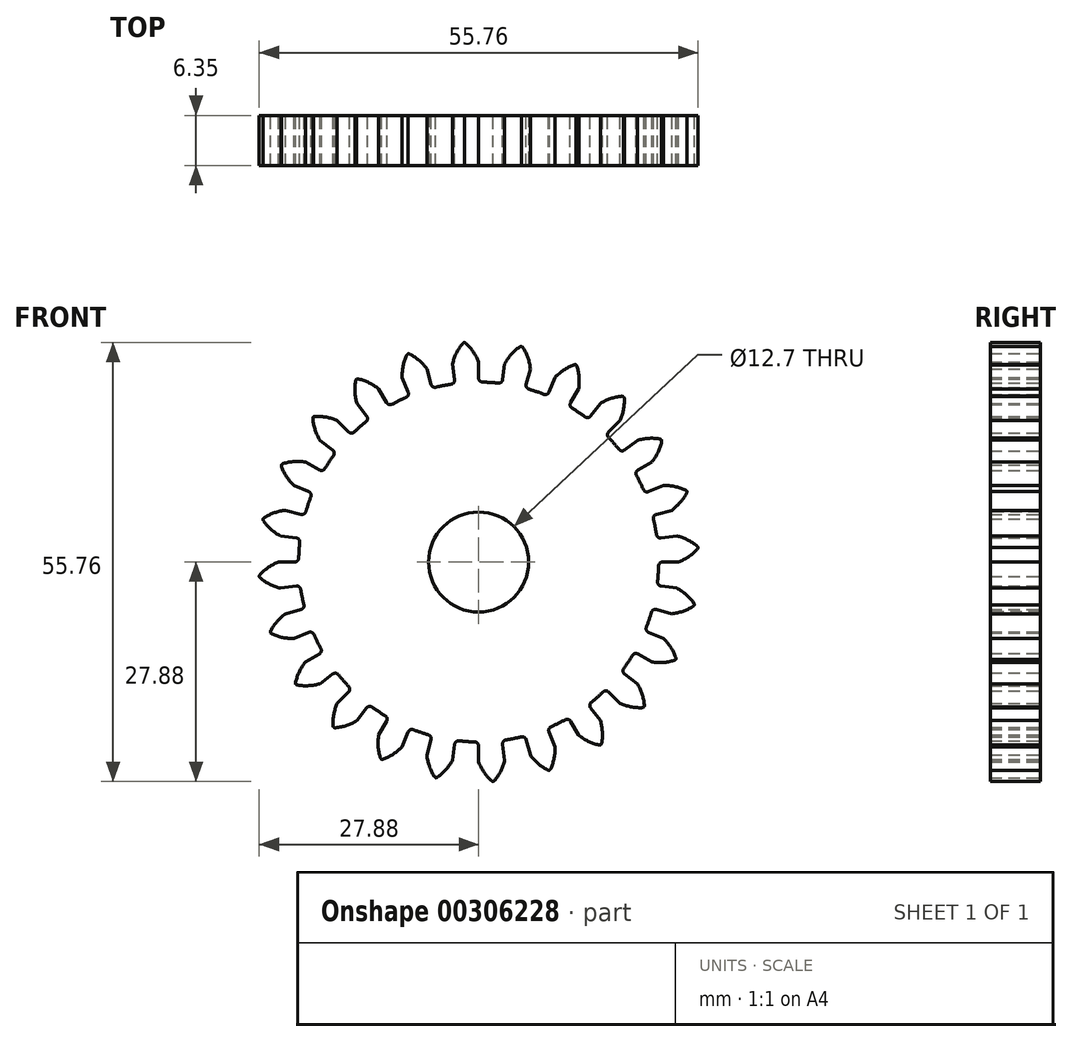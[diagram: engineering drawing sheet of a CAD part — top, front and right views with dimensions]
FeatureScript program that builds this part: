
annotation { "Feature Type Name" : "Feature", "Feature Type Description" : "" }
export const myFeature = defineFeature(function(context is Context, id is Id, definition is map)
    precondition{}
    {
        {
            var Q0;
            Q0=qCreatedBy(makeId("Front.planeOp"),FACE);
            var sketch = newSketch(context, id + "F0", { "sketchPlane" : qUnion([Q0])});
            skArc(sketch, "E0", {"start": v(-3.48, 22.6) * mm, "mid": v(1.5, -22.81) * mm, "end": v(0.5, 22.85) * mm});
            skLineSegment(sketch, "E1", {"start": v(0, 0) * mm, "end": v(-3, 45.83) * mm, "construction": true});
            skArc(sketch, "E2.trimOffspring", {"start": v(0, 25.4) * mm, "mid": v(-0.66, 26.66) * mm, "end": v(-1.58, 27.75) * mm});
            skLineSegment(sketch, "E3", {"start": v(0, 25.4) * mm, "end": v(0, 23.36) * mm});
            skArc(sketch, "E4.MirrorCS", {"start": v(-3.32, 25.18) * mm, "mid": v(-2.83, 26.52) * mm, "end": v(-2.06, 27.72) * mm});
            skLineSegment(sketch, "E5.MirrorCS", {"start": v(-3.32, 25.18) * mm, "end": v(-3.05, 23.16) * mm});
            skPoint(sketch, "E6.visualSharp", {"position": v(-1.92, 27.87) * mm});
            skArc(sketch, "E6.filletArc", {"start": v(-1.83, 27.88) * mm, "mid": v(-1.95, 27.81) * mm, "end": v(-2.06, 27.72) * mm});
            skPoint(sketch, "E7.visualSharp", {"position": v(-1.73, 27.89) * mm});
            skArc(sketch, "E7.filletArc", {"start": v(-1.58, 27.75) * mm, "mid": v(-1.7, 27.83) * mm, "end": v(-1.83, 27.88) * mm});
            skPoint(sketch, "E8.orphan", {"position": v(-2.55, 19.37) * mm});
            skPoint(sketch, "E9.orphan", {"position": v(0, 19.54) * mm});
            skPoint(sketch, "E10.visualSharp", {"position": v(-2.98, 22.66) * mm});
            skArc(sketch, "E10.filletArc", {"start": v(-3.48, 22.6) * mm, "mid": v(-3.15, 22.8) * mm, "end": v(-3.05, 23.16) * mm});
            skPoint(sketch, "E11.visualSharp", {"position": v(0, 22.86) * mm});
            skArc(sketch, "E11.filletArc", {"start": v(0, 23.36) * mm, "mid": v(0.14, 23) * mm, "end": v(0.5, 22.85) * mm});
            skPoint(sketch, "E12.MirrorCS.end.orphan", {"position": v(-1.83, 27.89) * mm});
            skArc(sketch, "E13.1.0", {"start": v(-6.57, 24.53) * mm, "mid": v(-7.54, 25.58) * mm, "end": v(-8.7, 26.4) * mm});
            skArc(sketch, "E13.1.1", {"start": v(-8.7, 26.4) * mm, "mid": v(-8.84, 26.44) * mm, "end": v(-8.98, 26.45) * mm});
            skArc(sketch, "E13.1.2", {"start": v(-8.98, 26.45) * mm, "mid": v(-9.08, 26.36) * mm, "end": v(-9.16, 26.24) * mm});
            skArc(sketch, "E13.1.3", {"start": v(-9.72, 23.47) * mm, "mid": v(-9.6, 24.89) * mm, "end": v(-9.16, 26.24) * mm});
            skLineSegment(sketch, "E13.1.4", {"start": v(-9.72, 23.47) * mm, "end": v(-8.94, 21.58) * mm});
            skArc(sketch, "E13.1.5", {"start": v(-9.2, 20.92) * mm, "mid": v(-8.94, 21.2) * mm, "end": v(-8.94, 21.58) * mm});
            skArc(sketch, "E13.1.6", {"start": v(-6.05, 22.57) * mm, "mid": v(-5.81, 22.26) * mm, "end": v(-5.44, 22.2) * mm});
            skLineSegment(sketch, "E13.1.7", {"start": v(-6.57, 24.53) * mm, "end": v(-6.05, 22.57) * mm});
            skArc(sketch, "E13.2.0", {"start": v(-12.7, 22) * mm, "mid": v(-13.9, 22.76) * mm, "end": v(-15.24, 23.24) * mm});
            skArc(sketch, "E13.2.1", {"start": v(-15.24, 23.24) * mm, "mid": v(-15.38, 23.25) * mm, "end": v(-15.52, 23.23) * mm});
            skArc(sketch, "E13.2.2", {"start": v(-15.52, 23.23) * mm, "mid": v(-15.6, 23.11) * mm, "end": v(-15.64, 22.98) * mm});
            skArc(sketch, "E13.2.3", {"start": v(-15.46, 20.15) * mm, "mid": v(-15.71, 21.55) * mm, "end": v(-15.64, 22.98) * mm});
            skLineSegment(sketch, "E13.2.4", {"start": v(-15.46, 20.15) * mm, "end": v(-14.22, 18.53) * mm});
            skArc(sketch, "E13.2.5", {"start": v(-14.3, 17.83) * mm, "mid": v(-14.12, 18.16) * mm, "end": v(-14.22, 18.53) * mm});
            skArc(sketch, "E13.2.6", {"start": v(-11.68, 20.23) * mm, "mid": v(-11.38, 20) * mm, "end": v(-11, 20.04) * mm});
            skLineSegment(sketch, "E13.2.7", {"start": v(-12.7, 22) * mm, "end": v(-11.68, 20.23) * mm});
            skArc(sketch, "E13.3.0", {"start": v(-17.96, 17.96) * mm, "mid": v(-19.32, 18.39) * mm, "end": v(-20.74, 18.5) * mm});
            skArc(sketch, "E13.3.1", {"start": v(-20.74, 18.5) * mm, "mid": v(-20.88, 18.48) * mm, "end": v(-21, 18.42) * mm});
            skArc(sketch, "E13.3.2", {"start": v(-21, 18.42) * mm, "mid": v(-21.05, 18.29) * mm, "end": v(-21.05, 18.14) * mm});
            skArc(sketch, "E13.3.3", {"start": v(-20.15, 15.46) * mm, "mid": v(-20.75, 16.75) * mm, "end": v(-21.05, 18.14) * mm});
            skLineSegment(sketch, "E13.3.4", {"start": v(-20.15, 15.46) * mm, "end": v(-18.53, 14.22) * mm});
            skArc(sketch, "E13.3.5", {"start": v(-18.43, 13.52) * mm, "mid": v(-18.34, 13.9) * mm, "end": v(-18.53, 14.22) * mm});
            skArc(sketch, "E13.3.6", {"start": v(-16.52, 16.52) * mm, "mid": v(-16.17, 16.37) * mm, "end": v(-15.8, 16.51) * mm});
            skLineSegment(sketch, "E13.3.7", {"start": v(-17.96, 17.96) * mm, "end": v(-16.52, 16.52) * mm});
            skArc(sketch, "E13.4.0", {"start": v(-22, 12.7) * mm, "mid": v(-23.42, 12.76) * mm, "end": v(-24.82, 12.5) * mm});
            skArc(sketch, "E13.4.1", {"start": v(-24.82, 12.5) * mm, "mid": v(-24.95, 12.45) * mm, "end": v(-25.06, 12.36) * mm});
            skArc(sketch, "E13.4.2", {"start": v(-25.06, 12.36) * mm, "mid": v(-25.06, 12.22) * mm, "end": v(-25.03, 12.08) * mm});
            skArc(sketch, "E13.4.3", {"start": v(-23.47, 9.72) * mm, "mid": v(-24.38, 10.81) * mm, "end": v(-25.03, 12.08) * mm});
            skLineSegment(sketch, "E13.4.4", {"start": v(-23.47, 9.72) * mm, "end": v(-21.58, 8.94) * mm});
            skArc(sketch, "E13.4.5", {"start": v(-21.3, 8.29) * mm, "mid": v(-21.31, 8.67) * mm, "end": v(-21.58, 8.94) * mm});
            skArc(sketch, "E13.4.6", {"start": v(-20.23, 11.68) * mm, "mid": v(-19.85, 11.63) * mm, "end": v(-19.54, 11.86) * mm});
            skLineSegment(sketch, "E13.4.7", {"start": v(-22, 12.7) * mm, "end": v(-20.23, 11.68) * mm});
            skArc(sketch, "E13.5.0", {"start": v(-24.53, 6.57) * mm, "mid": v(-25.92, 6.27) * mm, "end": v(-27.21, 5.66) * mm});
            skArc(sketch, "E13.5.1", {"start": v(-27.21, 5.66) * mm, "mid": v(-27.32, 5.57) * mm, "end": v(-27.4, 5.45) * mm});
            skArc(sketch, "E13.5.2", {"start": v(-27.4, 5.45) * mm, "mid": v(-27.37, 5.31) * mm, "end": v(-27.3, 5.19) * mm});
            skArc(sketch, "E13.5.3", {"start": v(-25.18, 3.32) * mm, "mid": v(-26.35, 4.13) * mm, "end": v(-27.3, 5.19) * mm});
            skLineSegment(sketch, "E13.5.4", {"start": v(-25.18, 3.32) * mm, "end": v(-23.16, 3.05) * mm});
            skArc(sketch, "E13.5.5", {"start": v(-22.72, 2.5) * mm, "mid": v(-22.83, 2.86) * mm, "end": v(-23.16, 3.05) * mm});
            skArc(sketch, "E13.5.6", {"start": v(-22.57, 6.05) * mm, "mid": v(-22.19, 6.1) * mm, "end": v(-21.95, 6.4) * mm});
            skLineSegment(sketch, "E13.5.7", {"start": v(-24.53, 6.57) * mm, "end": v(-22.57, 6.05) * mm});
            skArc(sketch, "E13.6.0", {"start": v(-25.4, 0) * mm, "mid": v(-26.66, -0.66) * mm, "end": v(-27.75, -1.58) * mm});
            skArc(sketch, "E13.6.1", {"start": v(-27.75, -1.58) * mm, "mid": v(-27.83, -1.7) * mm, "end": v(-27.88, -1.83) * mm});
            skArc(sketch, "E13.6.2", {"start": v(-27.88, -1.83) * mm, "mid": v(-27.81, -1.95) * mm, "end": v(-27.72, -2.06) * mm});
            skArc(sketch, "E13.6.3", {"start": v(-25.18, -3.32) * mm, "mid": v(-26.52, -2.83) * mm, "end": v(-27.72, -2.06) * mm});
            skLineSegment(sketch, "E13.6.4", {"start": v(-25.18, -3.32) * mm, "end": v(-23.16, -3.05) * mm});
            skArc(sketch, "E13.6.5", {"start": v(-22.6, -3.48) * mm, "mid": v(-22.8, -3.15) * mm, "end": v(-23.16, -3.05) * mm});
            skArc(sketch, "E13.6.6", {"start": v(-23.36, 0) * mm, "mid": v(-23, 0.14) * mm, "end": v(-22.85, 0.5) * mm});
            skLineSegment(sketch, "E13.6.7", {"start": v(-25.4, 0) * mm, "end": v(-23.36, 0) * mm});
            skArc(sketch, "E13.7.0", {"start": v(-24.53, -6.57) * mm, "mid": v(-25.58, -7.54) * mm, "end": v(-26.4, -8.7) * mm});
            skArc(sketch, "E13.7.1", {"start": v(-26.4, -8.7) * mm, "mid": v(-26.44, -8.84) * mm, "end": v(-26.45, -8.98) * mm});
            skArc(sketch, "E13.7.2", {"start": v(-26.45, -8.98) * mm, "mid": v(-26.36, -9.08) * mm, "end": v(-26.24, -9.16) * mm});
            skArc(sketch, "E13.7.3", {"start": v(-23.47, -9.72) * mm, "mid": v(-24.89, -9.6) * mm, "end": v(-26.24, -9.16) * mm});
            skLineSegment(sketch, "E13.7.4", {"start": v(-23.47, -9.72) * mm, "end": v(-21.58, -8.94) * mm});
            skArc(sketch, "E13.7.5", {"start": v(-20.92, -9.2) * mm, "mid": v(-21.2, -8.94) * mm, "end": v(-21.58, -8.94) * mm});
            skArc(sketch, "E13.7.6", {"start": v(-22.57, -6.05) * mm, "mid": v(-22.26, -5.81) * mm, "end": v(-22.2, -5.44) * mm});
            skLineSegment(sketch, "E13.7.7", {"start": v(-24.53, -6.57) * mm, "end": v(-22.57, -6.05) * mm});
            skArc(sketch, "E13.8.0", {"start": v(-22, -12.7) * mm, "mid": v(-22.76, -13.9) * mm, "end": v(-23.24, -15.24) * mm});
            skArc(sketch, "E13.8.1", {"start": v(-23.24, -15.24) * mm, "mid": v(-23.25, -15.38) * mm, "end": v(-23.23, -15.52) * mm});
            skArc(sketch, "E13.8.2", {"start": v(-23.23, -15.52) * mm, "mid": v(-23.11, -15.6) * mm, "end": v(-22.98, -15.64) * mm});
            skArc(sketch, "E13.8.3", {"start": v(-20.15, -15.46) * mm, "mid": v(-21.55, -15.71) * mm, "end": v(-22.98, -15.64) * mm});
            skLineSegment(sketch, "E13.8.4", {"start": v(-20.15, -15.46) * mm, "end": v(-18.53, -14.22) * mm});
            skArc(sketch, "E13.8.5", {"start": v(-17.83, -14.3) * mm, "mid": v(-18.16, -14.12) * mm, "end": v(-18.53, -14.22) * mm});
            skArc(sketch, "E13.8.6", {"start": v(-20.23, -11.68) * mm, "mid": v(-20, -11.38) * mm, "end": v(-20.04, -11) * mm});
            skLineSegment(sketch, "E13.8.7", {"start": v(-22, -12.7) * mm, "end": v(-20.23, -11.68) * mm});
            skArc(sketch, "E13.9.0", {"start": v(-17.96, -17.96) * mm, "mid": v(-18.39, -19.32) * mm, "end": v(-18.5, -20.74) * mm});
            skArc(sketch, "E13.9.1", {"start": v(-18.5, -20.74) * mm, "mid": v(-18.48, -20.88) * mm, "end": v(-18.42, -21) * mm});
            skArc(sketch, "E13.9.2", {"start": v(-18.42, -21) * mm, "mid": v(-18.29, -21.05) * mm, "end": v(-18.14, -21.05) * mm});
            skArc(sketch, "E13.9.3", {"start": v(-15.46, -20.15) * mm, "mid": v(-16.75, -20.75) * mm, "end": v(-18.14, -21.05) * mm});
            skLineSegment(sketch, "E13.9.4", {"start": v(-15.46, -20.15) * mm, "end": v(-14.22, -18.53) * mm});
            skArc(sketch, "E13.9.5", {"start": v(-13.52, -18.43) * mm, "mid": v(-13.9, -18.34) * mm, "end": v(-14.22, -18.53) * mm});
            skArc(sketch, "E13.9.6", {"start": v(-16.52, -16.52) * mm, "mid": v(-16.37, -16.17) * mm, "end": v(-16.51, -15.8) * mm});
            skLineSegment(sketch, "E13.9.7", {"start": v(-17.96, -17.96) * mm, "end": v(-16.52, -16.52) * mm});
            skArc(sketch, "E13.10.0", {"start": v(-12.7, -22) * mm, "mid": v(-12.76, -23.42) * mm, "end": v(-12.5, -24.82) * mm});
            skArc(sketch, "E13.10.1", {"start": v(-12.5, -24.82) * mm, "mid": v(-12.45, -24.95) * mm, "end": v(-12.36, -25.06) * mm});
            skArc(sketch, "E13.10.2", {"start": v(-12.36, -25.06) * mm, "mid": v(-12.22, -25.06) * mm, "end": v(-12.08, -25.03) * mm});
            skArc(sketch, "E13.10.3", {"start": v(-9.72, -23.47) * mm, "mid": v(-10.81, -24.38) * mm, "end": v(-12.08, -25.03) * mm});
            skLineSegment(sketch, "E13.10.4", {"start": v(-9.72, -23.47) * mm, "end": v(-8.94, -21.58) * mm});
            skArc(sketch, "E13.10.5", {"start": v(-8.29, -21.3) * mm, "mid": v(-8.67, -21.31) * mm, "end": v(-8.94, -21.58) * mm});
            skArc(sketch, "E13.10.6", {"start": v(-11.68, -20.23) * mm, "mid": v(-11.63, -19.85) * mm, "end": v(-11.86, -19.54) * mm});
            skLineSegment(sketch, "E13.10.7", {"start": v(-12.7, -22) * mm, "end": v(-11.68, -20.23) * mm});
            skArc(sketch, "E13.11.0", {"start": v(-6.57, -24.53) * mm, "mid": v(-6.27, -25.92) * mm, "end": v(-5.66, -27.21) * mm});
            skArc(sketch, "E13.11.1", {"start": v(-5.66, -27.21) * mm, "mid": v(-5.57, -27.32) * mm, "end": v(-5.45, -27.4) * mm});
            skArc(sketch, "E13.11.2", {"start": v(-5.45, -27.4) * mm, "mid": v(-5.31, -27.37) * mm, "end": v(-5.19, -27.3) * mm});
            skArc(sketch, "E13.11.3", {"start": v(-3.32, -25.18) * mm, "mid": v(-4.13, -26.35) * mm, "end": v(-5.19, -27.3) * mm});
            skLineSegment(sketch, "E13.11.4", {"start": v(-3.32, -25.18) * mm, "end": v(-3.05, -23.16) * mm});
            skArc(sketch, "E13.11.5", {"start": v(-2.5, -22.72) * mm, "mid": v(-2.86, -22.83) * mm, "end": v(-3.05, -23.16) * mm});
            skArc(sketch, "E13.11.6", {"start": v(-6.05, -22.57) * mm, "mid": v(-6.1, -22.19) * mm, "end": v(-6.4, -21.95) * mm});
            skLineSegment(sketch, "E13.11.7", {"start": v(-6.57, -24.53) * mm, "end": v(-6.05, -22.57) * mm});
            skArc(sketch, "E13.12.0", {"start": v(0, -25.4) * mm, "mid": v(0.66, -26.66) * mm, "end": v(1.58, -27.75) * mm});
            skArc(sketch, "E13.12.1", {"start": v(1.58, -27.75) * mm, "mid": v(1.7, -27.83) * mm, "end": v(1.83, -27.88) * mm});
            skArc(sketch, "E13.12.2", {"start": v(1.83, -27.88) * mm, "mid": v(1.95, -27.81) * mm, "end": v(2.06, -27.72) * mm});
            skArc(sketch, "E13.12.3", {"start": v(3.32, -25.18) * mm, "mid": v(2.83, -26.52) * mm, "end": v(2.06, -27.72) * mm});
            skLineSegment(sketch, "E13.12.4", {"start": v(3.32, -25.18) * mm, "end": v(3.05, -23.16) * mm});
            skArc(sketch, "E13.12.5", {"start": v(3.48, -22.6) * mm, "mid": v(3.15, -22.8) * mm, "end": v(3.05, -23.16) * mm});
            skArc(sketch, "E13.12.6", {"start": v(0, -23.36) * mm, "mid": v(-0.14, -23) * mm, "end": v(-0.5, -22.85) * mm});
            skLineSegment(sketch, "E13.12.7", {"start": v(0, -25.4) * mm, "end": v(0, -23.36) * mm});
            skArc(sketch, "E13.13.0", {"start": v(6.57, -24.53) * mm, "mid": v(7.54, -25.58) * mm, "end": v(8.7, -26.4) * mm});
            skArc(sketch, "E13.13.1", {"start": v(8.7, -26.4) * mm, "mid": v(8.84, -26.44) * mm, "end": v(8.98, -26.45) * mm});
            skArc(sketch, "E13.13.2", {"start": v(8.98, -26.45) * mm, "mid": v(9.08, -26.36) * mm, "end": v(9.16, -26.24) * mm});
            skArc(sketch, "E13.13.3", {"start": v(9.72, -23.47) * mm, "mid": v(9.6, -24.89) * mm, "end": v(9.16, -26.24) * mm});
            skLineSegment(sketch, "E13.13.4", {"start": v(9.72, -23.47) * mm, "end": v(8.94, -21.58) * mm});
            skArc(sketch, "E13.13.5", {"start": v(9.2, -20.92) * mm, "mid": v(8.94, -21.2) * mm, "end": v(8.94, -21.58) * mm});
            skArc(sketch, "E13.13.6", {"start": v(6.05, -22.57) * mm, "mid": v(5.81, -22.26) * mm, "end": v(5.44, -22.2) * mm});
            skLineSegment(sketch, "E13.13.7", {"start": v(6.57, -24.53) * mm, "end": v(6.05, -22.57) * mm});
            skArc(sketch, "E13.14.0", {"start": v(12.7, -22) * mm, "mid": v(13.9, -22.76) * mm, "end": v(15.24, -23.24) * mm});
            skArc(sketch, "E13.14.1", {"start": v(15.24, -23.24) * mm, "mid": v(15.38, -23.25) * mm, "end": v(15.52, -23.23) * mm});
            skArc(sketch, "E13.14.2", {"start": v(15.52, -23.23) * mm, "mid": v(15.6, -23.11) * mm, "end": v(15.64, -22.98) * mm});
            skArc(sketch, "E13.14.3", {"start": v(15.46, -20.15) * mm, "mid": v(15.71, -21.55) * mm, "end": v(15.64, -22.98) * mm});
            skLineSegment(sketch, "E13.14.4", {"start": v(15.46, -20.15) * mm, "end": v(14.22, -18.53) * mm});
            skArc(sketch, "E13.14.5", {"start": v(14.3, -17.83) * mm, "mid": v(14.12, -18.16) * mm, "end": v(14.22, -18.53) * mm});
            skArc(sketch, "E13.14.6", {"start": v(11.68, -20.23) * mm, "mid": v(11.38, -20) * mm, "end": v(11, -20.04) * mm});
            skLineSegment(sketch, "E13.14.7", {"start": v(12.7, -22) * mm, "end": v(11.68, -20.23) * mm});
            skArc(sketch, "E13.15.0", {"start": v(17.96, -17.96) * mm, "mid": v(19.32, -18.39) * mm, "end": v(20.74, -18.5) * mm});
            skArc(sketch, "E13.15.1", {"start": v(20.74, -18.5) * mm, "mid": v(20.88, -18.48) * mm, "end": v(21, -18.42) * mm});
            skArc(sketch, "E13.15.2", {"start": v(21, -18.42) * mm, "mid": v(21.05, -18.29) * mm, "end": v(21.05, -18.14) * mm});
            skArc(sketch, "E13.15.3", {"start": v(20.15, -15.46) * mm, "mid": v(20.75, -16.75) * mm, "end": v(21.05, -18.14) * mm});
            skLineSegment(sketch, "E13.15.4", {"start": v(20.15, -15.46) * mm, "end": v(18.53, -14.22) * mm});
            skArc(sketch, "E13.15.5", {"start": v(18.43, -13.52) * mm, "mid": v(18.34, -13.9) * mm, "end": v(18.53, -14.22) * mm});
            skArc(sketch, "E13.15.6", {"start": v(16.52, -16.52) * mm, "mid": v(16.17, -16.37) * mm, "end": v(15.8, -16.51) * mm});
            skLineSegment(sketch, "E13.15.7", {"start": v(17.96, -17.96) * mm, "end": v(16.52, -16.52) * mm});
            skArc(sketch, "E13.16.0", {"start": v(22, -12.7) * mm, "mid": v(23.42, -12.76) * mm, "end": v(24.82, -12.5) * mm});
            skArc(sketch, "E13.16.1", {"start": v(24.82, -12.5) * mm, "mid": v(24.95, -12.45) * mm, "end": v(25.06, -12.36) * mm});
            skArc(sketch, "E13.16.2", {"start": v(25.06, -12.36) * mm, "mid": v(25.06, -12.22) * mm, "end": v(25.03, -12.08) * mm});
            skArc(sketch, "E13.16.3", {"start": v(23.47, -9.72) * mm, "mid": v(24.38, -10.81) * mm, "end": v(25.03, -12.08) * mm});
            skLineSegment(sketch, "E13.16.4", {"start": v(23.47, -9.72) * mm, "end": v(21.58, -8.94) * mm});
            skArc(sketch, "E13.16.5", {"start": v(21.3, -8.29) * mm, "mid": v(21.31, -8.67) * mm, "end": v(21.58, -8.94) * mm});
            skArc(sketch, "E13.16.6", {"start": v(20.23, -11.68) * mm, "mid": v(19.85, -11.63) * mm, "end": v(19.54, -11.86) * mm});
            skLineSegment(sketch, "E13.16.7", {"start": v(22, -12.7) * mm, "end": v(20.23, -11.68) * mm});
            skArc(sketch, "E13.17.0", {"start": v(24.53, -6.57) * mm, "mid": v(25.92, -6.27) * mm, "end": v(27.21, -5.66) * mm});
            skArc(sketch, "E13.17.1", {"start": v(27.21, -5.66) * mm, "mid": v(27.32, -5.57) * mm, "end": v(27.4, -5.45) * mm});
            skArc(sketch, "E13.17.2", {"start": v(27.4, -5.45) * mm, "mid": v(27.37, -5.31) * mm, "end": v(27.3, -5.19) * mm});
            skArc(sketch, "E13.17.3", {"start": v(25.18, -3.32) * mm, "mid": v(26.35, -4.13) * mm, "end": v(27.3, -5.19) * mm});
            skLineSegment(sketch, "E13.17.4", {"start": v(25.18, -3.32) * mm, "end": v(23.16, -3.05) * mm});
            skArc(sketch, "E13.17.5", {"start": v(22.72, -2.5) * mm, "mid": v(22.83, -2.86) * mm, "end": v(23.16, -3.05) * mm});
            skArc(sketch, "E13.17.6", {"start": v(22.57, -6.05) * mm, "mid": v(22.19, -6.1) * mm, "end": v(21.95, -6.4) * mm});
            skLineSegment(sketch, "E13.17.7", {"start": v(24.53, -6.57) * mm, "end": v(22.57, -6.05) * mm});
            skArc(sketch, "E13.18.0", {"start": v(25.4, 0) * mm, "mid": v(26.66, 0.66) * mm, "end": v(27.75, 1.58) * mm});
            skArc(sketch, "E13.18.1", {"start": v(27.75, 1.58) * mm, "mid": v(27.83, 1.7) * mm, "end": v(27.88, 1.83) * mm});
            skArc(sketch, "E13.18.2", {"start": v(27.88, 1.83) * mm, "mid": v(27.81, 1.95) * mm, "end": v(27.72, 2.06) * mm});
            skArc(sketch, "E13.18.3", {"start": v(25.18, 3.32) * mm, "mid": v(26.52, 2.83) * mm, "end": v(27.72, 2.06) * mm});
            skLineSegment(sketch, "E13.18.4", {"start": v(25.18, 3.32) * mm, "end": v(23.16, 3.05) * mm});
            skArc(sketch, "E13.18.5", {"start": v(22.6, 3.48) * mm, "mid": v(22.8, 3.15) * mm, "end": v(23.16, 3.05) * mm});
            skArc(sketch, "E13.18.6", {"start": v(23.36, 0) * mm, "mid": v(23, -0.14) * mm, "end": v(22.85, -0.5) * mm});
            skLineSegment(sketch, "E13.18.7", {"start": v(25.4, 0) * mm, "end": v(23.36, 0) * mm});
            skArc(sketch, "E13.19.0", {"start": v(24.53, 6.57) * mm, "mid": v(25.58, 7.54) * mm, "end": v(26.4, 8.7) * mm});
            skArc(sketch, "E13.19.1", {"start": v(26.4, 8.7) * mm, "mid": v(26.44, 8.84) * mm, "end": v(26.45, 8.98) * mm});
            skArc(sketch, "E13.19.2", {"start": v(26.45, 8.98) * mm, "mid": v(26.36, 9.08) * mm, "end": v(26.24, 9.16) * mm});
            skArc(sketch, "E13.19.3", {"start": v(23.47, 9.72) * mm, "mid": v(24.89, 9.6) * mm, "end": v(26.24, 9.16) * mm});
            skLineSegment(sketch, "E13.19.4", {"start": v(23.47, 9.72) * mm, "end": v(21.58, 8.94) * mm});
            skArc(sketch, "E13.19.5", {"start": v(20.92, 9.2) * mm, "mid": v(21.2, 8.94) * mm, "end": v(21.58, 8.94) * mm});
            skArc(sketch, "E13.19.6", {"start": v(22.57, 6.05) * mm, "mid": v(22.26, 5.81) * mm, "end": v(22.2, 5.44) * mm});
            skLineSegment(sketch, "E13.19.7", {"start": v(24.53, 6.57) * mm, "end": v(22.57, 6.05) * mm});
            skArc(sketch, "E13.20.0", {"start": v(22, 12.7) * mm, "mid": v(22.76, 13.9) * mm, "end": v(23.24, 15.24) * mm});
            skArc(sketch, "E13.20.1", {"start": v(23.24, 15.24) * mm, "mid": v(23.25, 15.38) * mm, "end": v(23.23, 15.52) * mm});
            skArc(sketch, "E13.20.2", {"start": v(23.23, 15.52) * mm, "mid": v(23.11, 15.6) * mm, "end": v(22.98, 15.64) * mm});
            skArc(sketch, "E13.20.3", {"start": v(20.15, 15.46) * mm, "mid": v(21.55, 15.71) * mm, "end": v(22.98, 15.64) * mm});
            skLineSegment(sketch, "E13.20.4", {"start": v(20.15, 15.46) * mm, "end": v(18.53, 14.22) * mm});
            skArc(sketch, "E13.20.5", {"start": v(17.83, 14.3) * mm, "mid": v(18.16, 14.12) * mm, "end": v(18.53, 14.22) * mm});
            skArc(sketch, "E13.20.6", {"start": v(20.23, 11.68) * mm, "mid": v(20, 11.38) * mm, "end": v(20.04, 11) * mm});
            skLineSegment(sketch, "E13.20.7", {"start": v(22, 12.7) * mm, "end": v(20.23, 11.68) * mm});
            skArc(sketch, "E13.21.0", {"start": v(17.96, 17.96) * mm, "mid": v(18.39, 19.32) * mm, "end": v(18.5, 20.74) * mm});
            skArc(sketch, "E13.21.1", {"start": v(18.5, 20.74) * mm, "mid": v(18.48, 20.88) * mm, "end": v(18.42, 21) * mm});
            skArc(sketch, "E13.21.2", {"start": v(18.42, 21) * mm, "mid": v(18.29, 21.05) * mm, "end": v(18.14, 21.05) * mm});
            skArc(sketch, "E13.21.3", {"start": v(15.46, 20.15) * mm, "mid": v(16.75, 20.75) * mm, "end": v(18.14, 21.05) * mm});
            skLineSegment(sketch, "E13.21.4", {"start": v(15.46, 20.15) * mm, "end": v(14.22, 18.53) * mm});
            skArc(sketch, "E13.21.5", {"start": v(13.52, 18.43) * mm, "mid": v(13.9, 18.34) * mm, "end": v(14.22, 18.53) * mm});
            skArc(sketch, "E13.21.6", {"start": v(16.52, 16.52) * mm, "mid": v(16.37, 16.17) * mm, "end": v(16.51, 15.8) * mm});
            skLineSegment(sketch, "E13.21.7", {"start": v(17.96, 17.96) * mm, "end": v(16.52, 16.52) * mm});
            skArc(sketch, "E13.22.0", {"start": v(12.7, 22) * mm, "mid": v(12.76, 23.42) * mm, "end": v(12.5, 24.82) * mm});
            skArc(sketch, "E13.22.1", {"start": v(12.5, 24.82) * mm, "mid": v(12.45, 24.95) * mm, "end": v(12.36, 25.06) * mm});
            skArc(sketch, "E13.22.2", {"start": v(12.36, 25.06) * mm, "mid": v(12.22, 25.06) * mm, "end": v(12.08, 25.03) * mm});
            skArc(sketch, "E13.22.3", {"start": v(9.72, 23.47) * mm, "mid": v(10.81, 24.38) * mm, "end": v(12.08, 25.03) * mm});
            skLineSegment(sketch, "E13.22.4", {"start": v(9.72, 23.47) * mm, "end": v(8.94, 21.58) * mm});
            skArc(sketch, "E13.22.5", {"start": v(8.29, 21.3) * mm, "mid": v(8.67, 21.31) * mm, "end": v(8.94, 21.58) * mm});
            skArc(sketch, "E13.22.6", {"start": v(11.68, 20.23) * mm, "mid": v(11.63, 19.85) * mm, "end": v(11.86, 19.54) * mm});
            skLineSegment(sketch, "E13.22.7", {"start": v(12.7, 22) * mm, "end": v(11.68, 20.23) * mm});
            skArc(sketch, "E13.23.0", {"start": v(6.57, 24.53) * mm, "mid": v(6.27, 25.92) * mm, "end": v(5.66, 27.21) * mm});
            skArc(sketch, "E13.23.1", {"start": v(5.66, 27.21) * mm, "mid": v(5.57, 27.32) * mm, "end": v(5.45, 27.4) * mm});
            skArc(sketch, "E13.23.2", {"start": v(5.45, 27.4) * mm, "mid": v(5.31, 27.37) * mm, "end": v(5.19, 27.3) * mm});
            skArc(sketch, "E13.23.3", {"start": v(3.32, 25.18) * mm, "mid": v(4.13, 26.35) * mm, "end": v(5.19, 27.3) * mm});
            skLineSegment(sketch, "E13.23.4", {"start": v(3.32, 25.18) * mm, "end": v(3.05, 23.16) * mm});
            skArc(sketch, "E13.23.5", {"start": v(2.5, 22.72) * mm, "mid": v(2.86, 22.83) * mm, "end": v(3.05, 23.16) * mm});
            skArc(sketch, "E13.23.6", {"start": v(6.05, 22.57) * mm, "mid": v(6.1, 22.19) * mm, "end": v(6.4, 21.95) * mm});
            skLineSegment(sketch, "E13.23.7", {"start": v(6.57, 24.53) * mm, "end": v(6.05, 22.57) * mm});
            skSolve(sketch);
        }
        {
            var Q0;
            Q0 = qSketchRegion(id + "F0", true);
            extrude(context, id + "F1", {"entities" : qUnion([Q0]), "depth" : 6.35 * mm});
        }
        {
            var Q0;
            Q0=makeQuery(id+"F1.opExtrude","CAP_FACE",FACE,{"disambiguationData":[OSD([sQuery(id+"F0.wireOp",EDGE,"E0"),sQuery(id+"F0.wireOp",EDGE,"E2.trimOffspring"),sQuery(id+"F0.wireOp",EDGE,"E3"),sQuery(id+"F0.wireOp",EDGE,"E4.MirrorCS"),sQuery(id+"F0.wireOp",EDGE,"E5.MirrorCS"),sQuery(id+"F0.wireOp",EDGE,"E6.filletArc"),sQuery(id+"F0.wireOp",EDGE,"E7.filletArc"),sQuery(id+"F0.wireOp",EDGE,"E10.filletArc"),sQuery(id+"F0.wireOp",EDGE,"E11.filletArc"),sQuery(id+"F0.wireOp",EDGE,"E13.1.0"),sQuery(id+"F0.wireOp",EDGE,"E13.1.1"),sQuery(id+"F0.wireOp",EDGE,"E13.1.2"),sQuery(id+"F0.wireOp",EDGE,"E13.1.3"),sQuery(id+"F0.wireOp",EDGE,"E13.1.4"),sQuery(id+"F0.wireOp",EDGE,"E13.1.5"),sQuery(id+"F0.wireOp",EDGE,"E13.1.6"),sQuery(id+"F0.wireOp",EDGE,"E13.1.7"),sQuery(id+"F0.wireOp",EDGE,"E13.2.0"),sQuery(id+"F0.wireOp",EDGE,"E13.2.1"),sQuery(id+"F0.wireOp",EDGE,"E13.2.2"),sQuery(id+"F0.wireOp",EDGE,"E13.2.3"),sQuery(id+"F0.wireOp",EDGE,"E13.2.4"),sQuery(id+"F0.wireOp",EDGE,"E13.2.5"),sQuery(id+"F0.wireOp",EDGE,"E13.2.6"),sQuery(id+"F0.wireOp",EDGE,"E13.2.7"),sQuery(id+"F0.wireOp",EDGE,"E13.3.0"),sQuery(id+"F0.wireOp",EDGE,"E13.3.1"),sQuery(id+"F0.wireOp",EDGE,"E13.3.2"),sQuery(id+"F0.wireOp",EDGE,"E13.3.3"),sQuery(id+"F0.wireOp",EDGE,"E13.3.4"),sQuery(id+"F0.wireOp",EDGE,"E13.3.5"),sQuery(id+"F0.wireOp",EDGE,"E13.3.6"),sQuery(id+"F0.wireOp",EDGE,"E13.3.7"),sQuery(id+"F0.wireOp",EDGE,"E13.4.0"),sQuery(id+"F0.wireOp",EDGE,"E13.4.1"),sQuery(id+"F0.wireOp",EDGE,"E13.4.2"),sQuery(id+"F0.wireOp",EDGE,"E13.4.3"),sQuery(id+"F0.wireOp",EDGE,"E13.4.4"),sQuery(id+"F0.wireOp",EDGE,"E13.4.5"),sQuery(id+"F0.wireOp",EDGE,"E13.4.6"),sQuery(id+"F0.wireOp",EDGE,"E13.4.7"),sQuery(id+"F0.wireOp",EDGE,"E13.5.0"),sQuery(id+"F0.wireOp",EDGE,"E13.5.1"),sQuery(id+"F0.wireOp",EDGE,"E13.5.2"),sQuery(id+"F0.wireOp",EDGE,"E13.5.3"),sQuery(id+"F0.wireOp",EDGE,"E13.5.4"),sQuery(id+"F0.wireOp",EDGE,"E13.5.5"),sQuery(id+"F0.wireOp",EDGE,"E13.5.6"),sQuery(id+"F0.wireOp",EDGE,"E13.5.7"),sQuery(id+"F0.wireOp",EDGE,"E13.6.0"),sQuery(id+"F0.wireOp",EDGE,"E13.6.1"),sQuery(id+"F0.wireOp",EDGE,"E13.6.2"),sQuery(id+"F0.wireOp",EDGE,"E13.6.3"),sQuery(id+"F0.wireOp",EDGE,"E13.6.4"),sQuery(id+"F0.wireOp",EDGE,"E13.6.5"),sQuery(id+"F0.wireOp",EDGE,"E13.6.6"),sQuery(id+"F0.wireOp",EDGE,"E13.6.7"),sQuery(id+"F0.wireOp",EDGE,"E13.7.0"),sQuery(id+"F0.wireOp",EDGE,"E13.7.1"),sQuery(id+"F0.wireOp",EDGE,"E13.7.2"),sQuery(id+"F0.wireOp",EDGE,"E13.7.3"),sQuery(id+"F0.wireOp",EDGE,"E13.7.4"),sQuery(id+"F0.wireOp",EDGE,"E13.7.5"),sQuery(id+"F0.wireOp",EDGE,"E13.7.6"),sQuery(id+"F0.wireOp",EDGE,"E13.7.7"),sQuery(id+"F0.wireOp",EDGE,"E13.8.0"),sQuery(id+"F0.wireOp",EDGE,"E13.8.1"),sQuery(id+"F0.wireOp",EDGE,"E13.8.2"),sQuery(id+"F0.wireOp",EDGE,"E13.8.3"),sQuery(id+"F0.wireOp",EDGE,"E13.8.4"),sQuery(id+"F0.wireOp",EDGE,"E13.8.5"),sQuery(id+"F0.wireOp",EDGE,"E13.8.6"),sQuery(id+"F0.wireOp",EDGE,"E13.8.7"),sQuery(id+"F0.wireOp",EDGE,"E13.9.0"),sQuery(id+"F0.wireOp",EDGE,"E13.9.1"),sQuery(id+"F0.wireOp",EDGE,"E13.9.2"),sQuery(id+"F0.wireOp",EDGE,"E13.9.3"),sQuery(id+"F0.wireOp",EDGE,"E13.9.4"),sQuery(id+"F0.wireOp",EDGE,"E13.9.5"),sQuery(id+"F0.wireOp",EDGE,"E13.9.6"),sQuery(id+"F0.wireOp",EDGE,"E13.9.7"),sQuery(id+"F0.wireOp",EDGE,"E13.10.0"),sQuery(id+"F0.wireOp",EDGE,"E13.10.1"),sQuery(id+"F0.wireOp",EDGE,"E13.10.2"),sQuery(id+"F0.wireOp",EDGE,"E13.10.3"),sQuery(id+"F0.wireOp",EDGE,"E13.10.4"),sQuery(id+"F0.wireOp",EDGE,"E13.10.5"),sQuery(id+"F0.wireOp",EDGE,"E13.10.6"),sQuery(id+"F0.wireOp",EDGE,"E13.10.7"),sQuery(id+"F0.wireOp",EDGE,"E13.11.0"),sQuery(id+"F0.wireOp",EDGE,"E13.11.1"),sQuery(id+"F0.wireOp",EDGE,"E13.11.2"),sQuery(id+"F0.wireOp",EDGE,"E13.11.3"),sQuery(id+"F0.wireOp",EDGE,"E13.11.4"),sQuery(id+"F0.wireOp",EDGE,"E13.11.5"),sQuery(id+"F0.wireOp",EDGE,"E13.11.6"),sQuery(id+"F0.wireOp",EDGE,"E13.11.7"),sQuery(id+"F0.wireOp",EDGE,"E13.12.0"),sQuery(id+"F0.wireOp",EDGE,"E13.12.1"),sQuery(id+"F0.wireOp",EDGE,"E13.12.2"),sQuery(id+"F0.wireOp",EDGE,"E13.12.3"),sQuery(id+"F0.wireOp",EDGE,"E13.12.4"),sQuery(id+"F0.wireOp",EDGE,"E13.12.5"),sQuery(id+"F0.wireOp",EDGE,"E13.12.6"),sQuery(id+"F0.wireOp",EDGE,"E13.12.7"),sQuery(id+"F0.wireOp",EDGE,"E13.13.0"),sQuery(id+"F0.wireOp",EDGE,"E13.13.1"),sQuery(id+"F0.wireOp",EDGE,"E13.13.2"),sQuery(id+"F0.wireOp",EDGE,"E13.13.3"),sQuery(id+"F0.wireOp",EDGE,"E13.13.4"),sQuery(id+"F0.wireOp",EDGE,"E13.13.5"),sQuery(id+"F0.wireOp",EDGE,"E13.13.6"),sQuery(id+"F0.wireOp",EDGE,"E13.13.7"),sQuery(id+"F0.wireOp",EDGE,"E13.14.0"),sQuery(id+"F0.wireOp",EDGE,"E13.14.1"),sQuery(id+"F0.wireOp",EDGE,"E13.14.2"),sQuery(id+"F0.wireOp",EDGE,"E13.14.3"),sQuery(id+"F0.wireOp",EDGE,"E13.14.4"),sQuery(id+"F0.wireOp",EDGE,"E13.14.5"),sQuery(id+"F0.wireOp",EDGE,"E13.14.6"),sQuery(id+"F0.wireOp",EDGE,"E13.14.7"),sQuery(id+"F0.wireOp",EDGE,"E13.15.0"),sQuery(id+"F0.wireOp",EDGE,"E13.15.1"),sQuery(id+"F0.wireOp",EDGE,"E13.15.2"),sQuery(id+"F0.wireOp",EDGE,"E13.15.3"),sQuery(id+"F0.wireOp",EDGE,"E13.15.4"),sQuery(id+"F0.wireOp",EDGE,"E13.15.5"),sQuery(id+"F0.wireOp",EDGE,"E13.15.6"),sQuery(id+"F0.wireOp",EDGE,"E13.15.7"),sQuery(id+"F0.wireOp",EDGE,"E13.16.0"),sQuery(id+"F0.wireOp",EDGE,"E13.16.1"),sQuery(id+"F0.wireOp",EDGE,"E13.16.2"),sQuery(id+"F0.wireOp",EDGE,"E13.16.3"),sQuery(id+"F0.wireOp",EDGE,"E13.16.4"),sQuery(id+"F0.wireOp",EDGE,"E13.16.5"),sQuery(id+"F0.wireOp",EDGE,"E13.16.6"),sQuery(id+"F0.wireOp",EDGE,"E13.16.7"),sQuery(id+"F0.wireOp",EDGE,"E13.17.0"),sQuery(id+"F0.wireOp",EDGE,"E13.17.1"),sQuery(id+"F0.wireOp",EDGE,"E13.17.2"),sQuery(id+"F0.wireOp",EDGE,"E13.17.3"),sQuery(id+"F0.wireOp",EDGE,"E13.17.4"),sQuery(id+"F0.wireOp",EDGE,"E13.17.5"),sQuery(id+"F0.wireOp",EDGE,"E13.17.6"),sQuery(id+"F0.wireOp",EDGE,"E13.17.7"),sQuery(id+"F0.wireOp",EDGE,"E13.18.0"),sQuery(id+"F0.wireOp",EDGE,"E13.18.1"),sQuery(id+"F0.wireOp",EDGE,"E13.18.2"),sQuery(id+"F0.wireOp",EDGE,"E13.18.3"),sQuery(id+"F0.wireOp",EDGE,"E13.18.4"),sQuery(id+"F0.wireOp",EDGE,"E13.18.5"),sQuery(id+"F0.wireOp",EDGE,"E13.18.6"),sQuery(id+"F0.wireOp",EDGE,"E13.18.7"),sQuery(id+"F0.wireOp",EDGE,"E13.19.0"),sQuery(id+"F0.wireOp",EDGE,"E13.19.1"),sQuery(id+"F0.wireOp",EDGE,"E13.19.2"),sQuery(id+"F0.wireOp",EDGE,"E13.19.3"),sQuery(id+"F0.wireOp",EDGE,"E13.19.4"),sQuery(id+"F0.wireOp",EDGE,"E13.19.5"),sQuery(id+"F0.wireOp",EDGE,"E13.19.6"),sQuery(id+"F0.wireOp",EDGE,"E13.19.7"),sQuery(id+"F0.wireOp",EDGE,"E13.20.0"),sQuery(id+"F0.wireOp",EDGE,"E13.20.1"),sQuery(id+"F0.wireOp",EDGE,"E13.20.2"),sQuery(id+"F0.wireOp",EDGE,"E13.20.3"),sQuery(id+"F0.wireOp",EDGE,"E13.20.4"),sQuery(id+"F0.wireOp",EDGE,"E13.20.5"),sQuery(id+"F0.wireOp",EDGE,"E13.20.6"),sQuery(id+"F0.wireOp",EDGE,"E13.20.7"),sQuery(id+"F0.wireOp",EDGE,"E13.21.0"),sQuery(id+"F0.wireOp",EDGE,"E13.21.1"),sQuery(id+"F0.wireOp",EDGE,"E13.21.2"),sQuery(id+"F0.wireOp",EDGE,"E13.21.3"),sQuery(id+"F0.wireOp",EDGE,"E13.21.4"),sQuery(id+"F0.wireOp",EDGE,"E13.21.5"),sQuery(id+"F0.wireOp",EDGE,"E13.21.6"),sQuery(id+"F0.wireOp",EDGE,"E13.21.7"),sQuery(id+"F0.wireOp",EDGE,"E13.22.0"),sQuery(id+"F0.wireOp",EDGE,"E13.22.1"),sQuery(id+"F0.wireOp",EDGE,"E13.22.2"),sQuery(id+"F0.wireOp",EDGE,"E13.22.3"),sQuery(id+"F0.wireOp",EDGE,"E13.22.4"),sQuery(id+"F0.wireOp",EDGE,"E13.22.5"),sQuery(id+"F0.wireOp",EDGE,"E13.22.6"),sQuery(id+"F0.wireOp",EDGE,"E13.22.7"),sQuery(id+"F0.wireOp",EDGE,"E13.23.0"),sQuery(id+"F0.wireOp",EDGE,"E13.23.1"),sQuery(id+"F0.wireOp",EDGE,"E13.23.2"),sQuery(id+"F0.wireOp",EDGE,"E13.23.3"),sQuery(id+"F0.wireOp",EDGE,"E13.23.4"),sQuery(id+"F0.wireOp",EDGE,"E13.23.5"),sQuery(id+"F0.wireOp",EDGE,"E13.23.6"),sQuery(id+"F0.wireOp",EDGE,"E13.23.7")])],"isStart":false});
            var sketch = newSketch(context, id + "F2", { "sketchPlane" : qUnion([Q0])});
            skCircle(sketch, "E14", {"center": v(0, 0) * mm, "radius": 6.35 * mm});
            skSolve(sketch);
        }
        {
            var Q0;
            Q0 = qSketchRegion(id + "F2", true);
            extrude(context, id + "F3", {"entities" : qUnion([Q0]), "operationType" : NewBodyOperationType.REMOVE, "endBound" : BoundingType.THROUGH_ALL, "oppositeDirection" : true, "depth" : 25.4 * mm});
        }
    });
